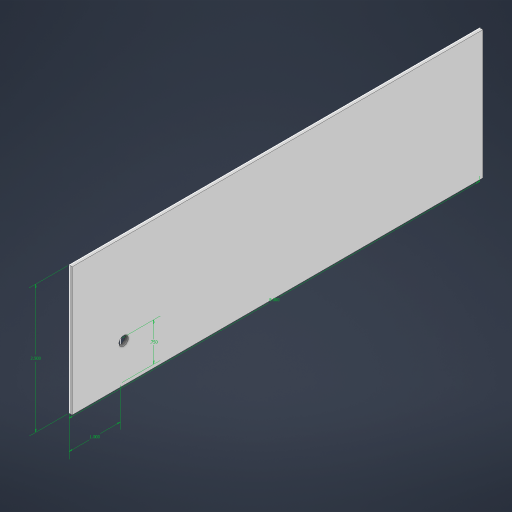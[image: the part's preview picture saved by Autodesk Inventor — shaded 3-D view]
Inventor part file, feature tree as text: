
AUTODESK INVENTOR PART (.ipt)
format: ipt  version: 2024 (Build 280153000, 153)  size: 172,544 bytes
history: native  units: in
note: dims shown in document units (in); Inventor stores cm internally (conversion verified against a paired STEP export)
features: sketch x1, extrude x1, hole x1
ambient origin geometry x8: Origin, YZ Plane, XZ Plane, XY Plane, X Axis, Y Axis, Z Axis, Center Point
bodies: Solid1 (feature_tree)
feature tree (3):
  sketch  "Sketch1"  dims[d0=8.0in d1=2.5in d2=1.0in d3=0.75in d4=0.0625in d5=0.0in d6=0.1875in d7=0.75in d8=0.375in d9=0.25in d10=0.5635in d11=1.0in d12=0.8108in]
  extrude  "Extrusion1"  Depth=2.5in
  hole  "Hole1"  [1 undecoded]
note: 1 required parameter value undecoded (feature->parameter linkage not recoverable at this tier; creation-order binding heuristic only, values carry confidence <= 0.55)
